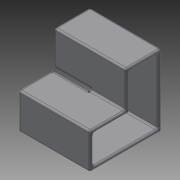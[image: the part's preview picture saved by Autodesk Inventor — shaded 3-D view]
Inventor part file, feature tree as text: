
AUTODESK INVENTOR PART (.ipt)
format: ipt  version: 2014 (Build 180170000, 170)  size: 300,032 bytes
history: native  units: in
note: dims shown in document units (in); Inventor stores cm internally (conversion verified against a paired STEP export)
features: plane x8, fillet x7, extrude x3, other x1, shell x1, sketch x1
ambient origin geometry x8: Origin, YZ Plane, XZ Plane, XY Plane, X Axis, Y Axis, Z Axis, Center Point
bodies: Body1 (feature_tree)
feature tree (21):
  other  "Cube Master.ipt"
  extrude  "Extrusion4"  Depth=0.3937in
  extrude  "Extrusion5"  Depth=0.0193in
  fillet  "Fillet1"  [1 undecoded]
  extrude  "Extrusion6"  Depth=0.0193in
  fillet  "Fillet2"  [1 undecoded]
  shell  "Shell1"  Thickness=0.374in
  fillet  "Fillet3"  [1 undecoded]
  fillet  "Fillet4"  Radius=0.0386in
  fillet  "Fillet7"  Radius=0.0386in
  fillet  "Fillet8"  Radius=0.0394in
  fillet  "Fillet9"  Radius=0.0193in
  sketch  "Sketch1"  dims[d0=0.3937in d1=0.3937in d9=0.374in d10=0.0in d11=0.374in d12=0.0in d13=0.374in d14=0.0in d15=0.0386in d16=0.0386in d17=0.0394in d18=0.0193in d19=0.0193in d22=0.0193in d23=0.0096in d24=0.0193in]
  plane  "Work Plane1"
  plane  "Work Plane2"
  plane  "Work Plane3"
  plane  "Work Plane4"
  plane  "Work Plane5"
  plane  "Work Plane6"
  plane  "Work Plane7"
  plane  "Work Plane8"
note: 3 required parameter values undecoded (feature->parameter linkage not recoverable at this tier; creation-order binding heuristic only, values carry confidence <= 0.55)
